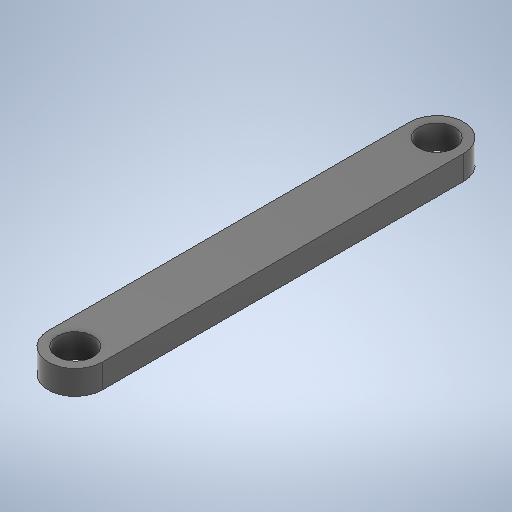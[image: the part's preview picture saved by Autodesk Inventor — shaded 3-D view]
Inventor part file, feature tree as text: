
AUTODESK INVENTOR PART (.ipt)
format: ipt  version: 2025.2 (Build 292293000, 293)  size: 235,008 bytes
history: native  units: mm
features: extrude x1, sketch x1
ambient origin geometry x8: Origin, YZ Plane, XZ Plane, XY Plane, X Axis, Y Axis, Z Axis, Center Point
bodies: Solid1 (feature_tree)
feature tree (2):
  extrude  "Extrusion1"  Depth=2.0mm
  sketch  "Sketch1"  dims[d0=4.5mm d1=30.0mm d2=3.0mm d3=2.0mm d4=0.0mm]
